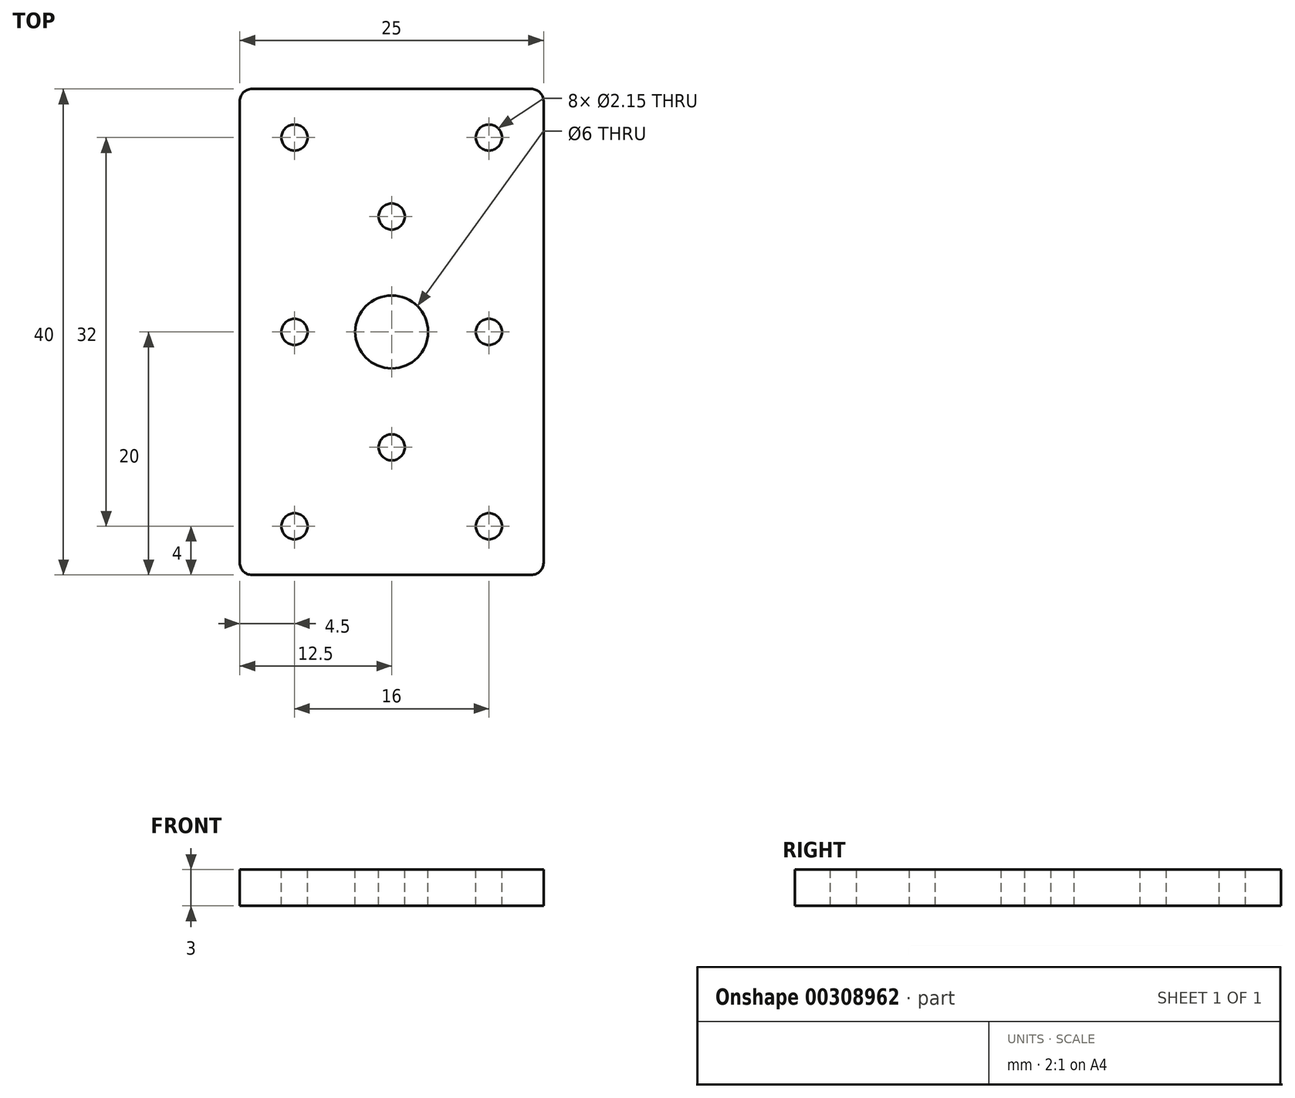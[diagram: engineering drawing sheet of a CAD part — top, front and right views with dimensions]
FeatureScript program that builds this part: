
annotation { "Feature Type Name" : "Feature", "Feature Type Description" : "" }
export const myFeature = defineFeature(function(context is Context, id is Id, definition is map)
    precondition{}
    {
        {
            var Q0;
            Q0=qCreatedBy(makeId("Top.planeOp"),FACE);
            var sketch = newSketch(context, id + "F0", { "sketchPlane" : qUnion([Q0])});
            skLineSegment(sketch, "E0.bottom", {"start": v(12.5, 20) * mm, "end": v(-12.5, 20) * mm});
            skLineSegment(sketch, "E0.top", {"start": v(12.5, -20) * mm, "end": v(-12.5, -20) * mm});
            skLineSegment(sketch, "E0.left", {"start": v(12.5, 20) * mm, "end": v(12.5, -20) * mm});
            skLineSegment(sketch, "E0.right", {"start": v(-12.5, 20) * mm, "end": v(-12.5, -20) * mm});
            skPoint(sketch, "E0.middle", {"position": v(0, 0) * mm});
            skSolve(sketch);
        }
        {
            var Q0;
            Q0=makeQuery(id+"F0.imprint","IMPRINT",FACE,{"disambiguationData":[TD([[makeQuery(id+"F0.imprint","IMPRINT",EDGE,{"derivedFrom":sQuery(id+"F0.wireOp",EDGE,"E0.bottom")}),1.0]])]});
            extrude(context, id + "F1", {"entities" : qUnion([Q0]), "offsetDistance" : 25 * mm, "depth" : 3 * mm});
        }
        {
            var Q0;
            Q0=makeQuery(id+"F1.opExtrude","CAP_FACE",FACE,{"disambiguationData":[OSD([sQuery(id+"F0.wireOp",EDGE,"E0.bottom"),sQuery(id+"F0.wireOp",EDGE,"E0.top"),sQuery(id+"F0.wireOp",EDGE,"E0.left"),sQuery(id+"F0.wireOp",EDGE,"E0.right")])],"isStart":false});
            var sketch = newSketch(context, id + "F2", { "sketchPlane" : qUnion([Q0])});
            skLineSegment(sketch, "E1", {"start": v(-8, 0) * mm, "end": v(8, 0) * mm});
            skLineSegment(sketch, "E2", {"start": v(0, -9.5) * mm, "end": v(0, 9.5) * mm});
            skLineSegment(sketch, "E3", {"start": v(8, 16) * mm, "end": v(-8, 16) * mm});
            skLineSegment(sketch, "E4", {"start": v(8, -16) * mm, "end": v(-8, -16) * mm});
            skSolve(sketch);
        }
        {
            var Q0;
            Q0=sQuery(id+"F2.wireOp",VERTEX,"E2.end");
            var Q1;
            Q1=sQuery(id+"F2.wireOp",VERTEX,"E2.start");
            var Q2;
            Q2=sQuery(id+"F2.wireOp",VERTEX,"E1.end");
            var Q3;
            Q3=sQuery(id+"F2.wireOp",VERTEX,"E1.start");
            var Q4;
            Q4=sQuery(id+"F2.wireOp",VERTEX,"E3.start");
            var Q5;
            Q5=sQuery(id+"F2.wireOp",VERTEX,"E3.end");
            var Q6;
            Q6=sQuery(id+"F2.wireOp",VERTEX,"E4.end");
            var Q7;
            Q7=sQuery(id+"F2.wireOp",VERTEX,"E4.start");
            var Q8;
            Q8=makeQuery(id+"F1.opExtrude","SWEPT_BODY",BODY,{"disambiguationData":[OSD([sQuery(id+"F0.wireOp",EDGE,"E0.bottom"),sQuery(id+"F0.wireOp",EDGE,"E0.top"),sQuery(id+"F0.wireOp",EDGE,"E0.left"),sQuery(id+"F0.wireOp",EDGE,"E0.right")])]});
            hole(context, id + "F3", {"style" : HoleStyle.SIMPLE, "endStyle" : HoleEndStyle.THROUGH, "standardTappedOrClearance" : lookupTablePath({ "standard" : "ISO", "engagement" : "75%", "pitch" : "0.35 mm", "size" : "M2.5", "type" : "Tapped" }), "standardBlindInLast" : lookupTablePath({ "standard" : "ISO", "fit" : "Normal", "engagement" : "75%", "pitch" : "0.35 mm", "size" : "M2.5", "type" : "Clearance & tapped" }), "holeDiameter" : 2.15 * mm, "majorDiameter" : 2.5 * mm, "showTappedDepth" : true, "tappedDepth" : 12 * mm, "tapClearance" : 3, "locations" : qUnion([Q0, Q1, Q2, Q3, Q4, Q5, Q6, Q7]), "scope" : qUnion([Q8])});
        }
        {
            var Q0;
            Q0=makeQuery(id+"F1.opExtrude","SWEPT_EDGE",EDGE,{"disambiguationData":[OSD([sQuery(id+"F0.wireOp",EDGE,"E0.top"),sQuery(id+"F0.wireOp",EDGE,"E0.left")])]});
            var Q1;
            Q1=makeQuery(id+"F1.opExtrude","SWEPT_EDGE",EDGE,{"disambiguationData":[OSD([sQuery(id+"F0.wireOp",EDGE,"E0.top"),sQuery(id+"F0.wireOp",EDGE,"E0.right")])]});
            var Q2;
            Q2=makeQuery(id+"F1.opExtrude","SWEPT_EDGE",EDGE,{"disambiguationData":[OSD([sQuery(id+"F0.wireOp",EDGE,"E0.bottom"),sQuery(id+"F0.wireOp",EDGE,"E0.left")])]});
            var Q3;
            Q3=makeQuery(id+"F1.opExtrude","SWEPT_EDGE",EDGE,{"disambiguationData":[OSD([sQuery(id+"F0.wireOp",EDGE,"E0.bottom"),sQuery(id+"F0.wireOp",EDGE,"E0.right")])]});
            fillet(context, id + "F4", {"entities" : qUnion([Q0, Q1, Q2, Q3]), "radius" : 1 * mm, "tangentPropagation" : true, "allowEdgeOverflow" : false});
        }
        {
            var Q0;
            Q0=makeQuery(id+"F1.opExtrude","CAP_FACE",FACE,{"disambiguationData":[OSD([sQuery(id+"F0.wireOp",EDGE,"E0.bottom"),sQuery(id+"F0.wireOp",EDGE,"E0.top"),sQuery(id+"F0.wireOp",EDGE,"E0.left"),sQuery(id+"F0.wireOp",EDGE,"E0.right")])],"isStart":false});
            var sketch = newSketch(context, id + "F5", { "sketchPlane" : qUnion([Q0])});
            skLineSegment(sketch, "E5", {"start": v(0, 0) * mm, "end": v(0, 2.66) * mm});
            skSolve(sketch);
        }
        {
            var Q0;
            Q0=sQuery(id+"F5.wireOp",VERTEX,"E5.start");
            var Q1;
            Q1=makeQuery(id+"F1.opExtrude","SWEPT_BODY",BODY,{"disambiguationData":[OSD([sQuery(id+"F0.wireOp",EDGE,"E0.bottom"),sQuery(id+"F0.wireOp",EDGE,"E0.top"),sQuery(id+"F0.wireOp",EDGE,"E0.left"),sQuery(id+"F0.wireOp",EDGE,"E0.right")])]});
            hole(context, id + "F6", {"style" : HoleStyle.SIMPLE, "endStyle" : HoleEndStyle.BLIND, "holeDiameter" : 6 * mm, "majorDiameter" : 3 * mm, "holeDepth" : 4.05 * mm, "tappedDepth" : 3 * mm, "tapClearance" : 3, "locations" : qUnion([Q0]), "scope" : qUnion([Q1])});
        }
    });
